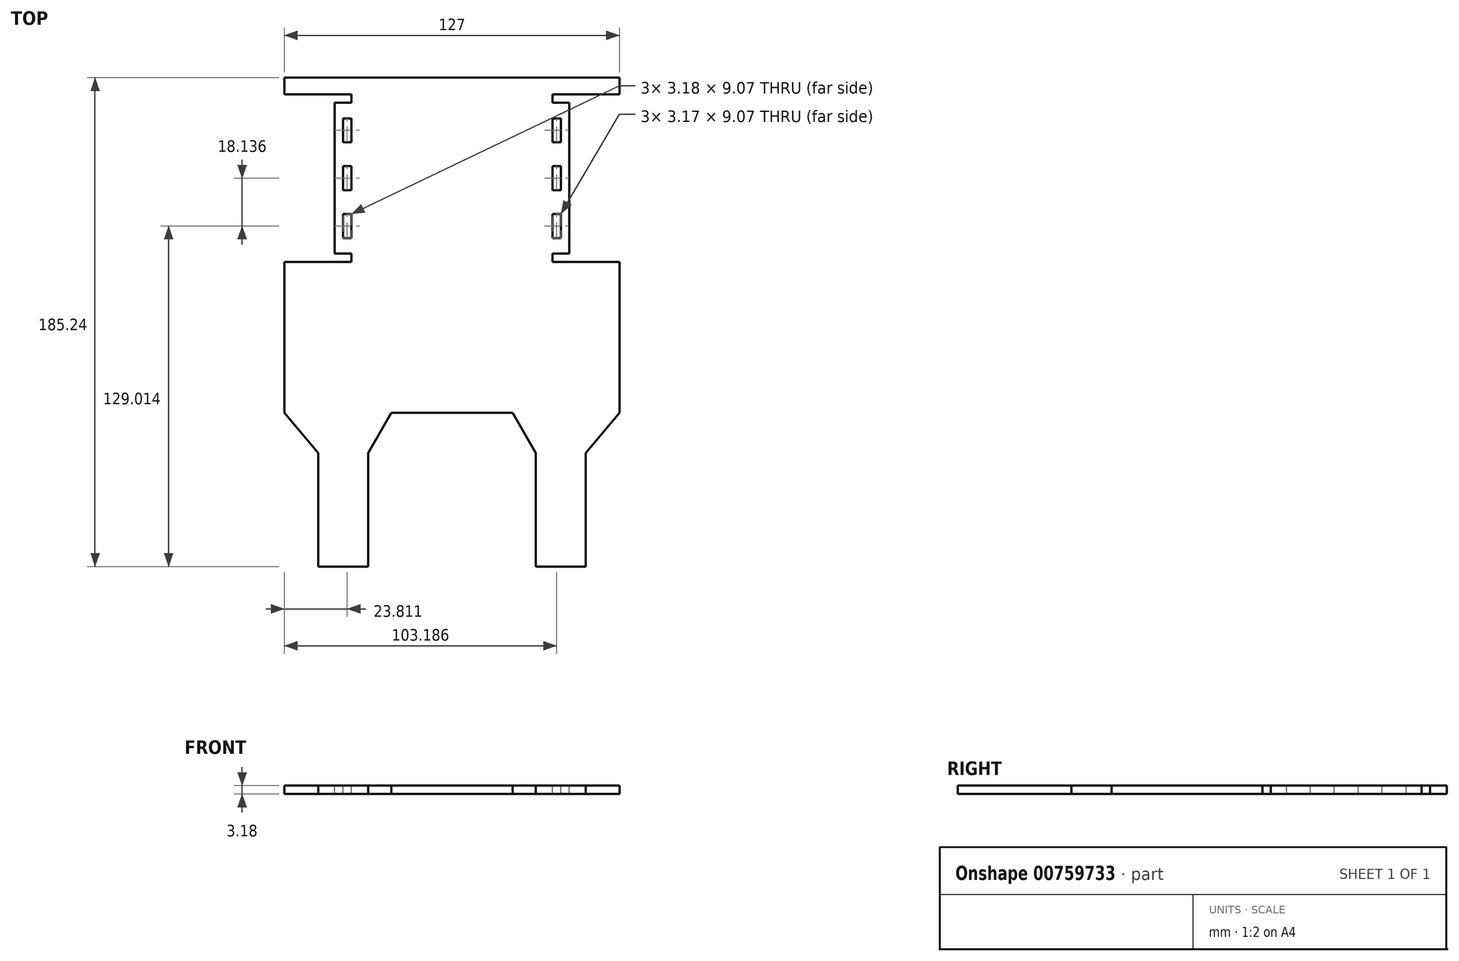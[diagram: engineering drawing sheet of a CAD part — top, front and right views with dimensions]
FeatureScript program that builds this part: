
annotation { "Feature Type Name" : "Feature", "Feature Type Description" : "" }
export const myFeature = defineFeature(function(context is Context, id is Id, definition is map)
    precondition{}
    {
        {
            var Q0;
            Q0=qCreatedBy(makeId("Top.planeOp"),FACE);
            var sketch = newSketch(context, id + "F0", { "sketchPlane" : qUnion([Q0])});
            skLineSegment(sketch, "E0.bottom", {"start": v(-114.18, -44.46) * mm, "end": v(-50.68, -44.46) * mm});
            skLineSegment(sketch, "E0.left", {"start": v(-114.18, -44.46) * mm, "end": v(-114.18, -171.46) * mm});
            skLineSegment(sketch, "E0.right", {"start": v(-50.68, -44.46) * mm, "end": v(-50.68, -171.46) * mm});
            skLineSegment(sketch, "E1", {"start": v(-114.18, -171.46) * mm, "end": v(-101.33, -186.66) * mm});
            skLineSegment(sketch, "E2", {"start": v(-101.33, -186.66) * mm, "end": v(-101.33, -229.7) * mm});
            skLineSegment(sketch, "E3", {"start": v(-101.33, -229.7) * mm, "end": v(-82.43, -229.7) * mm});
            skLineSegment(sketch, "E4", {"start": v(-82.43, -229.7) * mm, "end": v(-82.43, -186.66) * mm});
            skLineSegment(sketch, "E5", {"start": v(-82.43, -186.66) * mm, "end": v(-73.66, -171.46) * mm});
            skLineSegment(sketch, "E6", {"start": v(-73.66, -171.46) * mm, "end": v(-50.68, -171.46) * mm});
            skLineSegment(sketch, "E7", {"start": v(-50.68, -44.46) * mm, "end": v(-50.68, -229.7) * mm});
            skLineSegment(sketch, "E8.MirrorCS", {"start": v(-18.93, -229.7) * mm, "end": v(-18.93, -186.66) * mm});
            skLineSegment(sketch, "E9.MirrorCS", {"start": v(12.82, -171.46) * mm, "end": v(-0.04, -186.66) * mm});
            skLineSegment(sketch, "E10.MirrorCS", {"start": v(-0.04, -186.66) * mm, "end": v(-0.04, -229.7) * mm});
            skLineSegment(sketch, "E11.MirrorCS", {"start": v(-0.04, -229.7) * mm, "end": v(-18.93, -229.7) * mm});
            skLineSegment(sketch, "E12.MirrorCS", {"start": v(-18.93, -186.66) * mm, "end": v(-27.7, -171.46) * mm});
            skLineSegment(sketch, "E13.MirrorCS", {"start": v(12.82, -44.46) * mm, "end": v(12.82, -171.46) * mm});
            skLineSegment(sketch, "E14.MirrorCS", {"start": v(-27.7, -171.46) * mm, "end": v(-50.68, -171.46) * mm});
            skLineSegment(sketch, "E15.MirrorCS", {"start": v(12.82, -44.46) * mm, "end": v(-50.68, -44.46) * mm});
            skSolve(sketch);
        }
        {
            var Q0;
            Q0=makeQuery(id+"F0.imprint","IMPRINT",FACE,{"disambiguationData":[TD([[makeQuery(id+"F0.imprint","IMPRINT",EDGE,{"derivedFrom":sQuery(id+"F0.wireOp",EDGE,"E0.bottom")}),-1.0]])]});
            var Q1;
            Q1=makeQuery(id+"F0.imprint","IMPRINT",FACE,{"disambiguationData":[TD([[makeQuery(id+"F0.imprint","IMPRINT",EDGE,{"derivedFrom":sQuery(id+"F0.wireOp",EDGE,"E8.MirrorCS")}),-1.0]])]});
            extrude(context, id + "F1", {"entities" : qUnion([Q0, Q1]), "depth" : 3.17 * mm, "offsetDistance" : 25.4 * mm});
        }
        {
            var Q0;
            Q0=makeQuery(id+"F1.opExtrude","CAP_FACE",FACE,{"disambiguationData":[OSD([sQuery(id+"F0.wireOp",EDGE,"E0.bottom"),sQuery(id+"F0.wireOp",EDGE,"E0.left"),sQuery(id+"F0.wireOp",EDGE,"E1"),sQuery(id+"F0.wireOp",EDGE,"E2"),sQuery(id+"F0.wireOp",EDGE,"E3"),sQuery(id+"F0.wireOp",EDGE,"E4"),sQuery(id+"F0.wireOp",EDGE,"E5"),sQuery(id+"F0.wireOp",EDGE,"E6"),sQuery(id+"F0.wireOp",EDGE,"E8.MirrorCS"),sQuery(id+"F0.wireOp",EDGE,"E9.MirrorCS"),sQuery(id+"F0.wireOp",EDGE,"E10.MirrorCS"),sQuery(id+"F0.wireOp",EDGE,"E11.MirrorCS"),sQuery(id+"F0.wireOp",EDGE,"E12.MirrorCS"),sQuery(id+"F0.wireOp",EDGE,"E13.MirrorCS"),sQuery(id+"F0.wireOp",EDGE,"E14.MirrorCS"),sQuery(id+"F0.wireOp",EDGE,"E15.MirrorCS")])],"isStart":false});
            var sketch = newSketch(context, id + "F2", { "sketchPlane" : qUnion([Q0])});
            skSolve(sketch);
        }
        {
            var Q0;
            Q0=makeQuery(id+"F2.imprint","IMPRINT",FACE,{"disambiguationData":[TD([[makeQuery(id+"F2.imprint","IMPRINT",EDGE,{"derivedFrom":makeQuery(id+"F1.opExtrude","CAP_EDGE",EDGE,{"disambiguationData":[OSD([sQuery(id+"F0.wireOp",EDGE,"E0.left")])],"isStart":false})}),1.0]])]});
            var sketch = newSketch(context, id + "F3", { "sketchPlane" : qUnion([Q0])});
            skLineSegment(sketch, "E16", {"start": v(-111.64, -59.88) * mm, "end": v(-108.47, -59.88) * mm});
            skLineSegment(sketch, "E17", {"start": v(-108.47, -59.88) * mm, "end": v(-108.47, -68.95) * mm});
            skLineSegment(sketch, "E18", {"start": v(-108.47, -68.95) * mm, "end": v(-111.64, -68.95) * mm});
            skLineSegment(sketch, "E19", {"start": v(-111.64, -78.02) * mm, "end": v(-108.47, -78.02) * mm});
            skLineSegment(sketch, "E20", {"start": v(-108.47, -78.02) * mm, "end": v(-108.47, -87.08) * mm});
            skLineSegment(sketch, "E21", {"start": v(-108.47, -87.08) * mm, "end": v(-111.64, -87.08) * mm});
            skLineSegment(sketch, "E22", {"start": v(-111.64, -96.15) * mm, "end": v(-108.47, -96.15) * mm});
            skLineSegment(sketch, "E23", {"start": v(-108.47, -96.15) * mm, "end": v(-108.47, -105.22) * mm});
            skLineSegment(sketch, "E24", {"start": v(-108.47, -105.22) * mm, "end": v(-111.64, -105.22) * mm});
            skLineSegment(sketch, "E25", {"start": v(-111.64, -59.88) * mm, "end": v(-111.64, -68.95) * mm});
            skLineSegment(sketch, "E26", {"start": v(-111.64, -78.02) * mm, "end": v(-111.64, -87.08) * mm});
            skLineSegment(sketch, "E27", {"start": v(-111.64, -96.15) * mm, "end": v(-111.64, -105.22) * mm});
            skLineSegment(sketch, "E28.bottom", {"start": v(-91.96, -59.88) * mm, "end": v(-88.78, -59.88) * mm});
            skLineSegment(sketch, "E28.top", {"start": v(-91.96, -68.95) * mm, "end": v(-88.78, -68.95) * mm});
            skLineSegment(sketch, "E28.left", {"start": v(-91.96, -59.88) * mm, "end": v(-91.96, -68.95) * mm});
            skLineSegment(sketch, "E28.right", {"start": v(-88.78, -59.88) * mm, "end": v(-88.78, -68.95) * mm});
            skLineSegment(sketch, "E29.bottom", {"start": v(-91.96, -78.02) * mm, "end": v(-88.78, -78.02) * mm});
            skLineSegment(sketch, "E29.top", {"start": v(-91.96, -87.08) * mm, "end": v(-88.78, -87.08) * mm});
            skLineSegment(sketch, "E29.left", {"start": v(-91.96, -78.02) * mm, "end": v(-91.96, -87.08) * mm});
            skLineSegment(sketch, "E29.right", {"start": v(-88.78, -78.02) * mm, "end": v(-88.78, -87.08) * mm});
            skLineSegment(sketch, "E30.bottom", {"start": v(-91.96, -96.15) * mm, "end": v(-88.78, -96.15) * mm});
            skLineSegment(sketch, "E30.top", {"start": v(-91.96, -105.22) * mm, "end": v(-88.78, -105.22) * mm});
            skLineSegment(sketch, "E30.left", {"start": v(-91.96, -96.15) * mm, "end": v(-91.96, -105.22) * mm});
            skLineSegment(sketch, "E30.right", {"start": v(-88.78, -96.15) * mm, "end": v(-88.78, -105.22) * mm});
            skLineSegment(sketch, "E31", {"start": v(-50.68, -44.46) * mm, "end": v(-50.68, -199.38) * mm});
            skLineSegment(sketch, "E32.MirrorCS", {"start": v(-9.4, -78.02) * mm, "end": v(-12.58, -78.02) * mm});
            skLineSegment(sketch, "E33.MirrorCS", {"start": v(-9.4, -59.88) * mm, "end": v(-12.58, -59.88) * mm});
            skLineSegment(sketch, "E34.MirrorCS", {"start": v(7.1, -105.22) * mm, "end": v(10.28, -105.22) * mm});
            skLineSegment(sketch, "E35.MirrorCS", {"start": v(7.1, -78.02) * mm, "end": v(7.1, -87.08) * mm});
            skLineSegment(sketch, "E36.MirrorCS", {"start": v(-9.4, -105.22) * mm, "end": v(-12.58, -105.22) * mm});
            skLineSegment(sketch, "E37.MirrorCS", {"start": v(7.1, -87.08) * mm, "end": v(10.28, -87.08) * mm});
            skLineSegment(sketch, "E38.MirrorCS", {"start": v(-9.4, -68.95) * mm, "end": v(-12.58, -68.95) * mm});
            skLineSegment(sketch, "E39.MirrorCS", {"start": v(7.1, -68.95) * mm, "end": v(10.28, -68.95) * mm});
            skLineSegment(sketch, "E40.MirrorCS", {"start": v(-9.4, -87.08) * mm, "end": v(-12.58, -87.08) * mm});
            skLineSegment(sketch, "E41.MirrorCS", {"start": v(10.28, -59.88) * mm, "end": v(7.1, -59.88) * mm});
            skLineSegment(sketch, "E42.MirrorCS", {"start": v(-12.58, -59.88) * mm, "end": v(-12.58, -68.95) * mm});
            skLineSegment(sketch, "E43.MirrorCS", {"start": v(-12.58, -96.15) * mm, "end": v(-12.58, -105.22) * mm});
            skLineSegment(sketch, "E44.MirrorCS", {"start": v(-9.4, -96.15) * mm, "end": v(-9.4, -105.22) * mm});
            skLineSegment(sketch, "E45.MirrorCS", {"start": v(7.1, -96.15) * mm, "end": v(7.1, -105.22) * mm});
            skLineSegment(sketch, "E46.MirrorCS", {"start": v(-9.4, -96.15) * mm, "end": v(-12.58, -96.15) * mm});
            skLineSegment(sketch, "E47.MirrorCS", {"start": v(-12.58, -78.02) * mm, "end": v(-12.58, -87.08) * mm});
            skLineSegment(sketch, "E48.MirrorCS", {"start": v(7.1, -59.88) * mm, "end": v(7.1, -68.95) * mm});
            skLineSegment(sketch, "E49.MirrorCS", {"start": v(10.28, -59.88) * mm, "end": v(10.28, -68.95) * mm});
            skLineSegment(sketch, "E50.MirrorCS", {"start": v(-9.4, -78.02) * mm, "end": v(-9.4, -87.08) * mm});
            skLineSegment(sketch, "E51.MirrorCS", {"start": v(10.28, -78.02) * mm, "end": v(10.28, -87.08) * mm});
            skLineSegment(sketch, "E52.MirrorCS", {"start": v(10.28, -78.02) * mm, "end": v(7.1, -78.02) * mm});
            skLineSegment(sketch, "E53.MirrorCS", {"start": v(10.28, -96.15) * mm, "end": v(7.1, -96.15) * mm});
            skLineSegment(sketch, "E54.MirrorCS", {"start": v(-9.4, -59.88) * mm, "end": v(-9.4, -68.95) * mm});
            skLineSegment(sketch, "E55.MirrorCS", {"start": v(10.28, -96.15) * mm, "end": v(10.28, -105.22) * mm});
            skSolve(sketch);
        }
        {
            var Q0;
            Q0 = qSketchRegion(id + "F3", true);
            extrude(context, id + "F4", {"entities" : qUnion([Q0]), "operationType" : NewBodyOperationType.REMOVE, "oppositeDirection" : true, "depth" : 25.4 * mm, "offsetDistance" : 25.4 * mm});
        }
        {
            var Q0;
            Q0=makeQuery(id+"F2.imprint","IMPRINT",FACE,{"disambiguationData":[TD([[makeQuery(id+"F2.imprint","IMPRINT",EDGE,{"derivedFrom":makeQuery(id+"F1.opExtrude","CAP_EDGE",EDGE,{"disambiguationData":[OSD([sQuery(id+"F0.wireOp",EDGE,"E0.left")])],"isStart":false})}),1.0]])]});
            var sketch = newSketch(context, id + "F5", { "sketchPlane" : qUnion([Q0])});
            skLineSegment(sketch, "E56.bottom", {"start": v(-114.18, -50.81) * mm, "end": v(-95.13, -50.81) * mm});
            skLineSegment(sketch, "E56.top", {"start": v(-114.18, -114.31) * mm, "end": v(-95.13, -114.31) * mm});
            skLineSegment(sketch, "E56.left", {"start": v(-114.18, -50.81) * mm, "end": v(-114.18, -114.31) * mm});
            skLineSegment(sketch, "E56.right", {"start": v(-95.13, -53.99) * mm, "end": v(-95.13, -111.14) * mm});
            skLineSegment(sketch, "E57.bottom", {"start": v(-95.13, -114.31) * mm, "end": v(-88.78, -114.31) * mm});
            skLineSegment(sketch, "E57.top", {"start": v(-95.13, -111.14) * mm, "end": v(-88.78, -111.14) * mm});
            skLineSegment(sketch, "E57.right", {"start": v(-88.78, -114.31) * mm, "end": v(-88.78, -111.14) * mm});
            skLineSegment(sketch, "E58", {"start": v(-50.68, -44.46) * mm, "end": v(-50.68, -236.1) * mm});
            skLineSegment(sketch, "E59.MirrorCS", {"start": v(-12.58, -114.31) * mm, "end": v(-12.58, -111.14) * mm});
            skLineSegment(sketch, "E60.MirrorCS", {"start": v(12.82, -50.81) * mm, "end": v(-6.23, -50.81) * mm});
            skLineSegment(sketch, "E61.MirrorCS", {"start": v(12.82, -114.31) * mm, "end": v(-6.23, -114.31) * mm});
            skLineSegment(sketch, "E62.MirrorCS", {"start": v(12.82, -50.81) * mm, "end": v(12.82, -114.31) * mm});
            skLineSegment(sketch, "E63.MirrorCS", {"start": v(-6.23, -111.14) * mm, "end": v(-12.58, -111.14) * mm});
            skLineSegment(sketch, "E64.MirrorCS", {"start": v(-6.23, -114.31) * mm, "end": v(-12.58, -114.31) * mm});
            skLineSegment(sketch, "E65.MirrorCS", {"start": v(-6.23, -53.99) * mm, "end": v(-6.23, -111.14) * mm});
            skLineSegment(sketch, "E66.bottom", {"start": v(-88.78, -50.81) * mm, "end": v(-95.13, -50.81) * mm});
            skLineSegment(sketch, "E66.top", {"start": v(-88.78, -53.99) * mm, "end": v(-95.13, -53.99) * mm});
            skLineSegment(sketch, "E66.left", {"start": v(-88.78, -50.81) * mm, "end": v(-88.78, -53.99) * mm});
            skLineSegment(sketch, "E67.MirrorCS", {"start": v(-12.58, -50.81) * mm, "end": v(-12.58, -53.99) * mm});
            skLineSegment(sketch, "E68.MirrorCS", {"start": v(-12.58, -53.99) * mm, "end": v(-6.23, -53.99) * mm});
            skLineSegment(sketch, "E69.MirrorCS", {"start": v(-12.58, -50.81) * mm, "end": v(-6.23, -50.81) * mm});
            skSolve(sketch);
        }
        {
            var Q0;
            Q0 = qSketchRegion(id + "F5", true);
            extrude(context, id + "F6", {"entities" : qUnion([Q0]), "operationType" : NewBodyOperationType.REMOVE, "oppositeDirection" : true, "depth" : 25.4 * mm, "offsetDistance" : 25.4 * mm});
        }
    });
